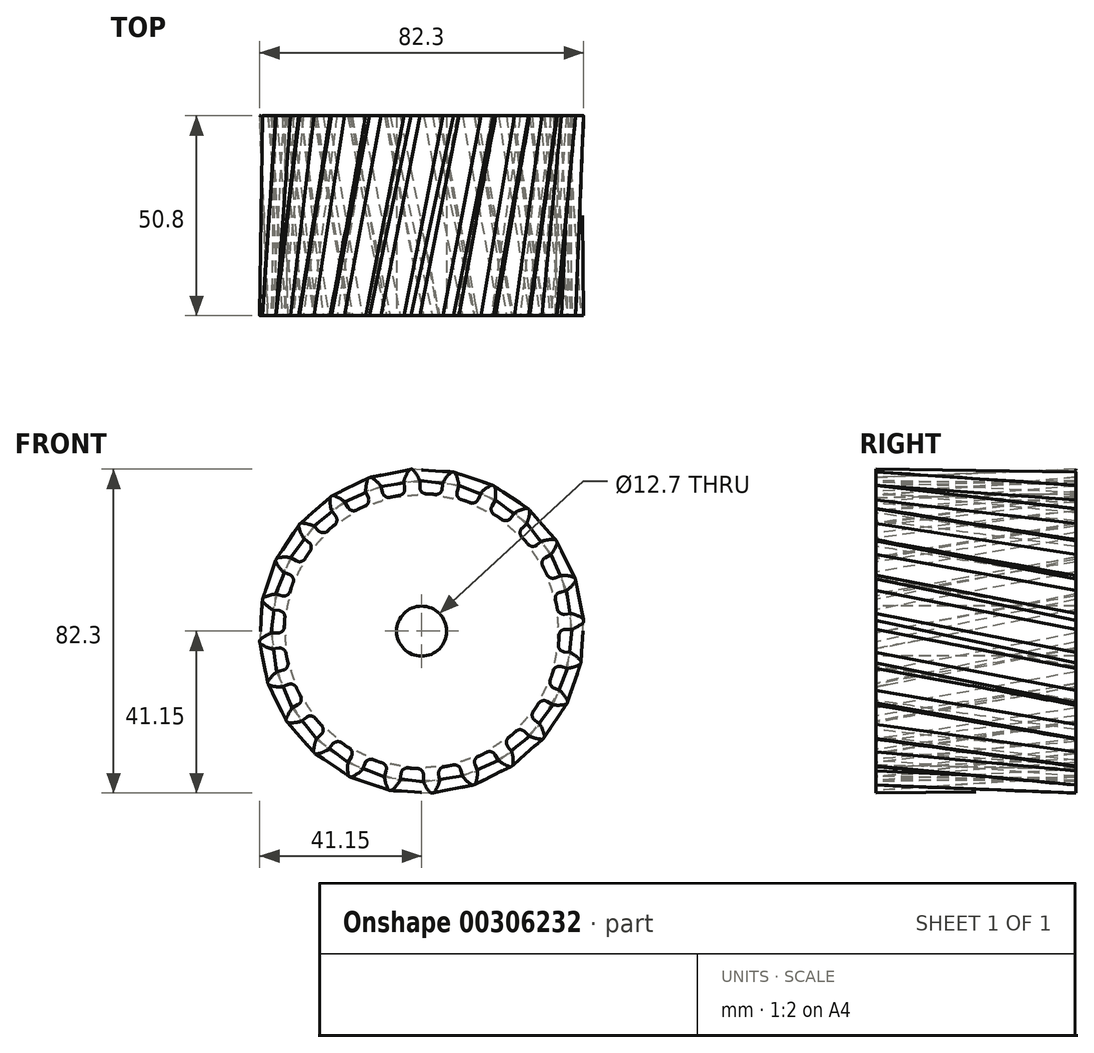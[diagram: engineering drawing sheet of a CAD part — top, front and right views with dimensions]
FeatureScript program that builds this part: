
annotation { "Feature Type Name" : "Feature", "Feature Type Description" : "" }
export const myFeature = defineFeature(function(context is Context, id is Id, definition is map)
    precondition{}
    {
        {
            var Q0;
            Q0=qCreatedBy(makeId("Front.planeOp"),FACE);
            var sketch = newSketch(context, id + "F0", { "sketchPlane" : qUnion([Q0])});
            skArc(sketch, "E0", {"start": v(-5.64, 34.47) * mm, "mid": v(-6.82, 34.25) * mm, "end": v(-7.99, 34) * mm});
            skLineSegment(sketch, "E1", {"start": v(0, 0) * mm, "end": v(-3.97, 60.48) * mm, "construction": true});
            skLineSegment(sketch, "E2", {"start": v(-2.53, 41.15) * mm, "end": v(-2.7, 41.15) * mm});
            skLineSegment(sketch, "E3", {"start": v(-0.47, 38.24) * mm, "end": v(-0.47, 36.5) * mm});
            skArc(sketch, "E4.trimOffspring", {"start": v(-0.47, 38.24) * mm, "mid": v(-1.2, 39.68) * mm, "end": v(-2.15, 40.98) * mm});
            skLineSegment(sketch, "E5.MirrorCS", {"start": v(-2.88, 41.13) * mm, "end": v(-2.7, 41.15) * mm});
            skArc(sketch, "E6.MirrorCS", {"start": v(-4.53, 37.97) * mm, "mid": v(-4, 39.5) * mm, "end": v(-3.23, 40.9) * mm});
            skLineSegment(sketch, "E7.MirrorCS", {"start": v(-4.53, 37.97) * mm, "end": v(-4.31, 36.25) * mm});
            skPoint(sketch, "E8.orphan", {"position": v(-3.52, 30.07) * mm});
            skPoint(sketch, "E9.orphan", {"position": v(-0.44, 30.27) * mm});
            skPoint(sketch, "E10.visualSharp", {"position": v(-3.1, 41.1) * mm});
            skArc(sketch, "E10.filletArc", {"start": v(-2.88, 41.13) * mm, "mid": v(-3.08, 41.06) * mm, "end": v(-3.23, 40.9) * mm});
            skPoint(sketch, "E11.visualSharp", {"position": v(-2.3, 41.15) * mm});
            skArc(sketch, "E11.filletArc", {"start": v(-2.15, 40.98) * mm, "mid": v(-2.32, 41.1) * mm, "end": v(-2.53, 41.15) * mm});
            skPoint(sketch, "E12.visualSharp", {"position": v(-4.11, 34.68) * mm});
            skArc(sketch, "E12.filletArc", {"start": v(-5.64, 34.47) * mm, "mid": v(-4.62, 35.09) * mm, "end": v(-4.31, 36.25) * mm});
            skPoint(sketch, "E13.visualSharp", {"position": v(-0.46, 34.92) * mm});
            skArc(sketch, "E13.filletArc", {"start": v(-0.47, 36.5) * mm, "mid": v(-0.01, 35.4) * mm, "end": v(1.08, 34.9) * mm});
            skLineSegment(sketch, "E14.1.0", {"start": v(-14.2, 35.5) * mm, "end": v(-13.55, 33.9) * mm});
            skArc(sketch, "E14.1.1", {"start": v(-14.37, 31.83) * mm, "mid": v(-13.54, 32.7) * mm, "end": v(-13.55, 33.9) * mm});
            skArc(sketch, "E14.1.2", {"start": v(-14.2, 35.5) * mm, "mid": v(-14.1, 37.11) * mm, "end": v(-13.7, 38.68) * mm});
            skArc(sketch, "E14.1.3", {"start": v(-13.42, 38.98) * mm, "mid": v(-13.6, 38.86) * mm, "end": v(-13.7, 38.68) * mm});
            skLineSegment(sketch, "E14.1.4", {"start": v(-13.42, 38.98) * mm, "end": v(-13.26, 39.05) * mm});
            skLineSegment(sketch, "E14.1.5", {"start": v(-13.1, 39.1) * mm, "end": v(-13.26, 39.05) * mm});
            skArc(sketch, "E14.1.6", {"start": v(-12.68, 39.03) * mm, "mid": v(-12.88, 39.1) * mm, "end": v(-13.1, 39.1) * mm});
            skArc(sketch, "E14.1.7", {"start": v(-10.35, 36.81) * mm, "mid": v(-11.42, 38.02) * mm, "end": v(-12.68, 39.03) * mm});
            skLineSegment(sketch, "E14.1.8", {"start": v(-10.35, 36.81) * mm, "end": v(-9.9, 35.14) * mm});
            skArc(sketch, "E14.1.9", {"start": v(-9.9, 35.14) * mm, "mid": v(-9.17, 34.18) * mm, "end": v(-7.99, 34) * mm});
            skLineSegment(sketch, "E14.2.0", {"start": v(-22.91, 30.62) * mm, "end": v(-21.86, 29.24) * mm});
            skArc(sketch, "E14.2.1", {"start": v(-22.12, 27.03) * mm, "mid": v(-21.54, 28.08) * mm, "end": v(-21.86, 29.24) * mm});
            skArc(sketch, "E14.2.2", {"start": v(-22.91, 30.62) * mm, "mid": v(-23.22, 32.2) * mm, "end": v(-23.25, 33.81) * mm});
            skArc(sketch, "E14.2.3", {"start": v(-23.05, 34.18) * mm, "mid": v(-23.2, 34.02) * mm, "end": v(-23.25, 33.81) * mm});
            skLineSegment(sketch, "E14.2.4", {"start": v(-23.05, 34.18) * mm, "end": v(-22.92, 34.29) * mm});
            skLineSegment(sketch, "E14.2.5", {"start": v(-22.77, 34.37) * mm, "end": v(-22.92, 34.29) * mm});
            skArc(sketch, "E14.2.6", {"start": v(-22.35, 34.42) * mm, "mid": v(-22.56, 34.44) * mm, "end": v(-22.77, 34.37) * mm});
            skArc(sketch, "E14.2.7", {"start": v(-19.53, 32.88) * mm, "mid": v(-20.87, 33.77) * mm, "end": v(-22.35, 34.42) * mm});
            skLineSegment(sketch, "E14.2.8", {"start": v(-19.53, 32.88) * mm, "end": v(-18.65, 31.38) * mm});
            skArc(sketch, "E14.2.9", {"start": v(-18.65, 31.38) * mm, "mid": v(-17.7, 30.64) * mm, "end": v(-16.51, 30.77) * mm});
            skLineSegment(sketch, "E14.3.0", {"start": v(-30.06, 23.65) * mm, "end": v(-28.68, 22.58) * mm});
            skArc(sketch, "E14.3.1", {"start": v(-28.36, 20.38) * mm, "mid": v(-28.08, 21.55) * mm, "end": v(-28.68, 22.58) * mm});
            skArc(sketch, "E14.3.2", {"start": v(-30.06, 23.65) * mm, "mid": v(-30.76, 25.1) * mm, "end": v(-31.21, 26.64) * mm});
            skArc(sketch, "E14.3.3", {"start": v(-31.12, 27.05) * mm, "mid": v(-31.2, 26.86) * mm, "end": v(-31.21, 26.64) * mm});
            skLineSegment(sketch, "E14.3.4", {"start": v(-31.12, 27.05) * mm, "end": v(-31.01, 27.19) * mm});
            skLineSegment(sketch, "E14.3.5", {"start": v(-30.89, 27.31) * mm, "end": v(-31.01, 27.19) * mm});
            skArc(sketch, "E14.3.6", {"start": v(-30.5, 27.46) * mm, "mid": v(-30.7, 27.43) * mm, "end": v(-30.89, 27.31) * mm});
            skArc(sketch, "E14.3.7", {"start": v(-27.37, 26.7) * mm, "mid": v(-28.9, 27.22) * mm, "end": v(-30.5, 27.46) * mm});
            skLineSegment(sketch, "E14.3.8", {"start": v(-27.37, 26.7) * mm, "end": v(-26.14, 25.48) * mm});
            skArc(sketch, "E14.3.9", {"start": v(-26.14, 25.48) * mm, "mid": v(-25.03, 25.02) * mm, "end": v(-23.92, 25.45) * mm});
            skLineSegment(sketch, "E14.4.0", {"start": v(-35.15, 15.06) * mm, "end": v(-33.55, 14.39) * mm});
            skArc(sketch, "E14.4.1", {"start": v(-32.67, 12.35) * mm, "mid": v(-32.7, 13.55) * mm, "end": v(-33.55, 14.39) * mm});
            skArc(sketch, "E14.4.2", {"start": v(-35.15, 15.06) * mm, "mid": v(-36.2, 16.28) * mm, "end": v(-37.04, 17.66) * mm});
            skArc(sketch, "E14.4.3", {"start": v(-37.06, 18.07) * mm, "mid": v(-37.1, 17.86) * mm, "end": v(-37.04, 17.66) * mm});
            skLineSegment(sketch, "E14.4.4", {"start": v(-37.06, 18.07) * mm, "end": v(-37, 18.24) * mm});
            skLineSegment(sketch, "E14.4.5", {"start": v(-36.9, 18.39) * mm, "end": v(-37, 18.24) * mm});
            skArc(sketch, "E14.4.6", {"start": v(-36.56, 18.63) * mm, "mid": v(-36.76, 18.54) * mm, "end": v(-36.9, 18.39) * mm});
            skArc(sketch, "E14.4.7", {"start": v(-33.35, 18.7) * mm, "mid": v(-34.96, 18.8) * mm, "end": v(-36.56, 18.63) * mm});
            skLineSegment(sketch, "E14.4.8", {"start": v(-33.35, 18.7) * mm, "end": v(-31.84, 17.85) * mm});
            skArc(sketch, "E14.4.9", {"start": v(-31.84, 17.85) * mm, "mid": v(-30.66, 17.69) * mm, "end": v(-29.69, 18.4) * mm});
            skLineSegment(sketch, "E14.5.0", {"start": v(-37.85, 5.45) * mm, "end": v(-36.13, 5.22) * mm});
            skArc(sketch, "E14.5.1", {"start": v(-34.75, 3.47) * mm, "mid": v(-35.09, 4.62) * mm, "end": v(-36.13, 5.22) * mm});
            skArc(sketch, "E14.5.2", {"start": v(-37.85, 5.45) * mm, "mid": v(-39.19, 6.35) * mm, "end": v(-40.35, 7.47) * mm});
            skArc(sketch, "E14.5.3", {"start": v(-40.47, 7.87) * mm, "mid": v(-40.45, 7.65) * mm, "end": v(-40.35, 7.47) * mm});
            skLineSegment(sketch, "E14.5.4", {"start": v(-40.47, 7.87) * mm, "end": v(-40.45, 8.04) * mm});
            skLineSegment(sketch, "E14.5.5", {"start": v(-40.4, 8.2) * mm, "end": v(-40.45, 8.04) * mm});
            skArc(sketch, "E14.5.6", {"start": v(-40.14, 8.53) * mm, "mid": v(-40.3, 8.4) * mm, "end": v(-40.4, 8.2) * mm});
            skArc(sketch, "E14.5.7", {"start": v(-37.06, 9.44) * mm, "mid": v(-38.64, 9.12) * mm, "end": v(-40.14, 8.53) * mm});
            skLineSegment(sketch, "E14.5.8", {"start": v(-37.06, 9.44) * mm, "end": v(-35.38, 9) * mm});
            skArc(sketch, "E14.5.9", {"start": v(-35.38, 9) * mm, "mid": v(-34.19, 9.15) * mm, "end": v(-33.44, 10.08) * mm});
            skLineSegment(sketch, "E14.6.0", {"start": v(-37.97, -4.53) * mm, "end": v(-36.25, -4.31) * mm});
            skArc(sketch, "E14.6.1", {"start": v(-34.47, -5.64) * mm, "mid": v(-35.09, -4.62) * mm, "end": v(-36.25, -4.31) * mm});
            skArc(sketch, "E14.6.2", {"start": v(-37.97, -4.53) * mm, "mid": v(-39.5, -4) * mm, "end": v(-40.9, -3.23) * mm});
            skArc(sketch, "E14.6.3", {"start": v(-41.13, -2.88) * mm, "mid": v(-41.06, -3.08) * mm, "end": v(-40.9, -3.23) * mm});
            skLineSegment(sketch, "E14.6.4", {"start": v(-41.13, -2.88) * mm, "end": v(-41.15, -2.7) * mm});
            skLineSegment(sketch, "E14.6.5", {"start": v(-41.15, -2.53) * mm, "end": v(-41.15, -2.7) * mm});
            skArc(sketch, "E14.6.6", {"start": v(-40.98, -2.15) * mm, "mid": v(-41.1, -2.32) * mm, "end": v(-41.15, -2.53) * mm});
            skArc(sketch, "E14.6.7", {"start": v(-38.24, -0.47) * mm, "mid": v(-39.68, -1.2) * mm, "end": v(-40.98, -2.15) * mm});
            skLineSegment(sketch, "E14.6.8", {"start": v(-38.24, -0.47) * mm, "end": v(-36.5, -0.47) * mm});
            skArc(sketch, "E14.6.9", {"start": v(-36.5, -0.47) * mm, "mid": v(-35.4, -0.01) * mm, "end": v(-34.9, 1.08) * mm});
            skLineSegment(sketch, "E14.7.0", {"start": v(-35.5, -14.2) * mm, "end": v(-33.9, -13.55) * mm});
            skArc(sketch, "E14.7.1", {"start": v(-31.83, -14.37) * mm, "mid": v(-32.7, -13.54) * mm, "end": v(-33.9, -13.55) * mm});
            skArc(sketch, "E14.7.2", {"start": v(-35.5, -14.2) * mm, "mid": v(-37.11, -14.1) * mm, "end": v(-38.68, -13.7) * mm});
            skArc(sketch, "E14.7.3", {"start": v(-38.98, -13.42) * mm, "mid": v(-38.86, -13.6) * mm, "end": v(-38.68, -13.7) * mm});
            skLineSegment(sketch, "E14.7.4", {"start": v(-38.98, -13.42) * mm, "end": v(-39.05, -13.26) * mm});
            skLineSegment(sketch, "E14.7.5", {"start": v(-39.1, -13.1) * mm, "end": v(-39.05, -13.26) * mm});
            skArc(sketch, "E14.7.6", {"start": v(-39.03, -12.68) * mm, "mid": v(-39.1, -12.88) * mm, "end": v(-39.1, -13.1) * mm});
            skArc(sketch, "E14.7.7", {"start": v(-36.81, -10.35) * mm, "mid": v(-38.02, -11.42) * mm, "end": v(-39.03, -12.68) * mm});
            skLineSegment(sketch, "E14.7.8", {"start": v(-36.81, -10.35) * mm, "end": v(-35.14, -9.9) * mm});
            skArc(sketch, "E14.7.9", {"start": v(-35.14, -9.9) * mm, "mid": v(-34.18, -9.17) * mm, "end": v(-34, -7.99) * mm});
            skLineSegment(sketch, "E14.8.0", {"start": v(-30.62, -22.91) * mm, "end": v(-29.24, -21.86) * mm});
            skArc(sketch, "E14.8.1", {"start": v(-27.03, -22.12) * mm, "mid": v(-28.08, -21.54) * mm, "end": v(-29.24, -21.86) * mm});
            skArc(sketch, "E14.8.2", {"start": v(-30.62, -22.91) * mm, "mid": v(-32.2, -23.22) * mm, "end": v(-33.81, -23.25) * mm});
            skArc(sketch, "E14.8.3", {"start": v(-34.18, -23.05) * mm, "mid": v(-34.02, -23.2) * mm, "end": v(-33.81, -23.25) * mm});
            skLineSegment(sketch, "E14.8.4", {"start": v(-34.18, -23.05) * mm, "end": v(-34.29, -22.92) * mm});
            skLineSegment(sketch, "E14.8.5", {"start": v(-34.37, -22.77) * mm, "end": v(-34.29, -22.92) * mm});
            skArc(sketch, "E14.8.6", {"start": v(-34.42, -22.35) * mm, "mid": v(-34.44, -22.56) * mm, "end": v(-34.37, -22.77) * mm});
            skArc(sketch, "E14.8.7", {"start": v(-32.88, -19.53) * mm, "mid": v(-33.77, -20.87) * mm, "end": v(-34.42, -22.35) * mm});
            skLineSegment(sketch, "E14.8.8", {"start": v(-32.88, -19.53) * mm, "end": v(-31.38, -18.65) * mm});
            skArc(sketch, "E14.8.9", {"start": v(-31.38, -18.65) * mm, "mid": v(-30.64, -17.7) * mm, "end": v(-30.77, -16.51) * mm});
            skLineSegment(sketch, "E14.9.0", {"start": v(-23.65, -30.06) * mm, "end": v(-22.58, -28.68) * mm});
            skArc(sketch, "E14.9.1", {"start": v(-20.38, -28.36) * mm, "mid": v(-21.55, -28.08) * mm, "end": v(-22.58, -28.68) * mm});
            skArc(sketch, "E14.9.2", {"start": v(-23.65, -30.06) * mm, "mid": v(-25.1, -30.76) * mm, "end": v(-26.64, -31.21) * mm});
            skArc(sketch, "E14.9.3", {"start": v(-27.05, -31.12) * mm, "mid": v(-26.86, -31.2) * mm, "end": v(-26.64, -31.21) * mm});
            skLineSegment(sketch, "E14.9.4", {"start": v(-27.05, -31.12) * mm, "end": v(-27.19, -31.01) * mm});
            skLineSegment(sketch, "E14.9.5", {"start": v(-27.31, -30.89) * mm, "end": v(-27.19, -31.01) * mm});
            skArc(sketch, "E14.9.6", {"start": v(-27.46, -30.5) * mm, "mid": v(-27.43, -30.7) * mm, "end": v(-27.31, -30.89) * mm});
            skArc(sketch, "E14.9.7", {"start": v(-26.7, -27.37) * mm, "mid": v(-27.22, -28.9) * mm, "end": v(-27.46, -30.5) * mm});
            skLineSegment(sketch, "E14.9.8", {"start": v(-26.7, -27.37) * mm, "end": v(-25.48, -26.14) * mm});
            skArc(sketch, "E14.9.9", {"start": v(-25.48, -26.14) * mm, "mid": v(-25.02, -25.03) * mm, "end": v(-25.45, -23.92) * mm});
            skLineSegment(sketch, "E14.10.0", {"start": v(-15.06, -35.15) * mm, "end": v(-14.39, -33.55) * mm});
            skArc(sketch, "E14.10.1", {"start": v(-12.35, -32.67) * mm, "mid": v(-13.55, -32.7) * mm, "end": v(-14.39, -33.55) * mm});
            skArc(sketch, "E14.10.2", {"start": v(-15.06, -35.15) * mm, "mid": v(-16.28, -36.2) * mm, "end": v(-17.66, -37.04) * mm});
            skArc(sketch, "E14.10.3", {"start": v(-18.07, -37.06) * mm, "mid": v(-17.86, -37.1) * mm, "end": v(-17.66, -37.04) * mm});
            skLineSegment(sketch, "E14.10.4", {"start": v(-18.07, -37.06) * mm, "end": v(-18.24, -37) * mm});
            skLineSegment(sketch, "E14.10.5", {"start": v(-18.39, -36.9) * mm, "end": v(-18.24, -37) * mm});
            skArc(sketch, "E14.10.6", {"start": v(-18.63, -36.56) * mm, "mid": v(-18.54, -36.76) * mm, "end": v(-18.39, -36.9) * mm});
            skArc(sketch, "E14.10.7", {"start": v(-18.7, -33.35) * mm, "mid": v(-18.8, -34.96) * mm, "end": v(-18.63, -36.56) * mm});
            skLineSegment(sketch, "E14.10.8", {"start": v(-18.7, -33.35) * mm, "end": v(-17.85, -31.84) * mm});
            skArc(sketch, "E14.10.9", {"start": v(-17.85, -31.84) * mm, "mid": v(-17.69, -30.66) * mm, "end": v(-18.4, -29.69) * mm});
            skLineSegment(sketch, "E14.11.0", {"start": v(-5.45, -37.85) * mm, "end": v(-5.22, -36.13) * mm});
            skArc(sketch, "E14.11.1", {"start": v(-3.47, -34.75) * mm, "mid": v(-4.62, -35.09) * mm, "end": v(-5.22, -36.13) * mm});
            skArc(sketch, "E14.11.2", {"start": v(-5.45, -37.85) * mm, "mid": v(-6.35, -39.19) * mm, "end": v(-7.47, -40.35) * mm});
            skArc(sketch, "E14.11.3", {"start": v(-7.87, -40.47) * mm, "mid": v(-7.65, -40.45) * mm, "end": v(-7.47, -40.35) * mm});
            skLineSegment(sketch, "E14.11.4", {"start": v(-7.87, -40.47) * mm, "end": v(-8.04, -40.45) * mm});
            skLineSegment(sketch, "E14.11.5", {"start": v(-8.2, -40.4) * mm, "end": v(-8.04, -40.45) * mm});
            skArc(sketch, "E14.11.6", {"start": v(-8.53, -40.14) * mm, "mid": v(-8.4, -40.3) * mm, "end": v(-8.2, -40.4) * mm});
            skArc(sketch, "E14.11.7", {"start": v(-9.44, -37.06) * mm, "mid": v(-9.12, -38.64) * mm, "end": v(-8.53, -40.14) * mm});
            skLineSegment(sketch, "E14.11.8", {"start": v(-9.44, -37.06) * mm, "end": v(-9, -35.38) * mm});
            skArc(sketch, "E14.11.9", {"start": v(-9, -35.38) * mm, "mid": v(-9.15, -34.19) * mm, "end": v(-10.08, -33.44) * mm});
            skLineSegment(sketch, "E14.12.0", {"start": v(4.53, -37.97) * mm, "end": v(4.31, -36.25) * mm});
            skArc(sketch, "E14.12.1", {"start": v(5.64, -34.47) * mm, "mid": v(4.62, -35.09) * mm, "end": v(4.31, -36.25) * mm});
            skArc(sketch, "E14.12.2", {"start": v(4.53, -37.97) * mm, "mid": v(4, -39.5) * mm, "end": v(3.23, -40.9) * mm});
            skArc(sketch, "E14.12.3", {"start": v(2.88, -41.13) * mm, "mid": v(3.08, -41.06) * mm, "end": v(3.23, -40.9) * mm});
            skLineSegment(sketch, "E14.12.4", {"start": v(2.88, -41.13) * mm, "end": v(2.7, -41.15) * mm});
            skLineSegment(sketch, "E14.12.5", {"start": v(2.53, -41.15) * mm, "end": v(2.7, -41.15) * mm});
            skArc(sketch, "E14.12.6", {"start": v(2.15, -40.98) * mm, "mid": v(2.32, -41.1) * mm, "end": v(2.53, -41.15) * mm});
            skArc(sketch, "E14.12.7", {"start": v(0.47, -38.24) * mm, "mid": v(1.2, -39.68) * mm, "end": v(2.15, -40.98) * mm});
            skLineSegment(sketch, "E14.12.8", {"start": v(0.47, -38.24) * mm, "end": v(0.47, -36.5) * mm});
            skArc(sketch, "E14.12.9", {"start": v(0.47, -36.5) * mm, "mid": v(0.01, -35.4) * mm, "end": v(-1.08, -34.9) * mm});
            skLineSegment(sketch, "E14.13.0", {"start": v(14.2, -35.5) * mm, "end": v(13.55, -33.9) * mm});
            skArc(sketch, "E14.13.1", {"start": v(14.37, -31.83) * mm, "mid": v(13.54, -32.7) * mm, "end": v(13.55, -33.9) * mm});
            skArc(sketch, "E14.13.2", {"start": v(14.2, -35.5) * mm, "mid": v(14.1, -37.11) * mm, "end": v(13.7, -38.68) * mm});
            skArc(sketch, "E14.13.3", {"start": v(13.42, -38.98) * mm, "mid": v(13.6, -38.86) * mm, "end": v(13.7, -38.68) * mm});
            skLineSegment(sketch, "E14.13.4", {"start": v(13.42, -38.98) * mm, "end": v(13.26, -39.05) * mm});
            skLineSegment(sketch, "E14.13.5", {"start": v(13.1, -39.1) * mm, "end": v(13.26, -39.05) * mm});
            skArc(sketch, "E14.13.6", {"start": v(12.68, -39.03) * mm, "mid": v(12.88, -39.1) * mm, "end": v(13.1, -39.1) * mm});
            skArc(sketch, "E14.13.7", {"start": v(10.35, -36.81) * mm, "mid": v(11.42, -38.02) * mm, "end": v(12.68, -39.03) * mm});
            skLineSegment(sketch, "E14.13.8", {"start": v(10.35, -36.81) * mm, "end": v(9.9, -35.14) * mm});
            skArc(sketch, "E14.13.9", {"start": v(9.9, -35.14) * mm, "mid": v(9.17, -34.18) * mm, "end": v(7.99, -34) * mm});
            skLineSegment(sketch, "E14.14.0", {"start": v(22.91, -30.62) * mm, "end": v(21.86, -29.24) * mm});
            skArc(sketch, "E14.14.1", {"start": v(22.12, -27.03) * mm, "mid": v(21.54, -28.08) * mm, "end": v(21.86, -29.24) * mm});
            skArc(sketch, "E14.14.2", {"start": v(22.91, -30.62) * mm, "mid": v(23.22, -32.2) * mm, "end": v(23.25, -33.81) * mm});
            skArc(sketch, "E14.14.3", {"start": v(23.05, -34.18) * mm, "mid": v(23.2, -34.02) * mm, "end": v(23.25, -33.81) * mm});
            skLineSegment(sketch, "E14.14.4", {"start": v(23.05, -34.18) * mm, "end": v(22.92, -34.29) * mm});
            skLineSegment(sketch, "E14.14.5", {"start": v(22.77, -34.37) * mm, "end": v(22.92, -34.29) * mm});
            skArc(sketch, "E14.14.6", {"start": v(22.35, -34.42) * mm, "mid": v(22.56, -34.44) * mm, "end": v(22.77, -34.37) * mm});
            skArc(sketch, "E14.14.7", {"start": v(19.53, -32.88) * mm, "mid": v(20.87, -33.77) * mm, "end": v(22.35, -34.42) * mm});
            skLineSegment(sketch, "E14.14.8", {"start": v(19.53, -32.88) * mm, "end": v(18.65, -31.38) * mm});
            skArc(sketch, "E14.14.9", {"start": v(18.65, -31.38) * mm, "mid": v(17.7, -30.64) * mm, "end": v(16.51, -30.77) * mm});
            skLineSegment(sketch, "E14.15.0", {"start": v(30.06, -23.65) * mm, "end": v(28.68, -22.58) * mm});
            skArc(sketch, "E14.15.1", {"start": v(28.36, -20.38) * mm, "mid": v(28.08, -21.55) * mm, "end": v(28.68, -22.58) * mm});
            skArc(sketch, "E14.15.2", {"start": v(30.06, -23.65) * mm, "mid": v(30.76, -25.1) * mm, "end": v(31.21, -26.64) * mm});
            skArc(sketch, "E14.15.3", {"start": v(31.12, -27.05) * mm, "mid": v(31.2, -26.86) * mm, "end": v(31.21, -26.64) * mm});
            skLineSegment(sketch, "E14.15.4", {"start": v(31.12, -27.05) * mm, "end": v(31.01, -27.19) * mm});
            skLineSegment(sketch, "E14.15.5", {"start": v(30.89, -27.31) * mm, "end": v(31.01, -27.19) * mm});
            skArc(sketch, "E14.15.6", {"start": v(30.5, -27.46) * mm, "mid": v(30.7, -27.43) * mm, "end": v(30.89, -27.31) * mm});
            skArc(sketch, "E14.15.7", {"start": v(27.37, -26.7) * mm, "mid": v(28.9, -27.22) * mm, "end": v(30.5, -27.46) * mm});
            skLineSegment(sketch, "E14.15.8", {"start": v(27.37, -26.7) * mm, "end": v(26.14, -25.48) * mm});
            skArc(sketch, "E14.15.9", {"start": v(26.14, -25.48) * mm, "mid": v(25.03, -25.02) * mm, "end": v(23.92, -25.45) * mm});
            skLineSegment(sketch, "E14.16.0", {"start": v(35.15, -15.06) * mm, "end": v(33.55, -14.39) * mm});
            skArc(sketch, "E14.16.1", {"start": v(32.67, -12.35) * mm, "mid": v(32.7, -13.55) * mm, "end": v(33.55, -14.39) * mm});
            skArc(sketch, "E14.16.2", {"start": v(35.15, -15.06) * mm, "mid": v(36.2, -16.28) * mm, "end": v(37.04, -17.66) * mm});
            skArc(sketch, "E14.16.3", {"start": v(37.06, -18.07) * mm, "mid": v(37.1, -17.86) * mm, "end": v(37.04, -17.66) * mm});
            skLineSegment(sketch, "E14.16.4", {"start": v(37.06, -18.07) * mm, "end": v(37, -18.24) * mm});
            skLineSegment(sketch, "E14.16.5", {"start": v(36.9, -18.39) * mm, "end": v(37, -18.24) * mm});
            skArc(sketch, "E14.16.6", {"start": v(36.56, -18.63) * mm, "mid": v(36.76, -18.54) * mm, "end": v(36.9, -18.39) * mm});
            skArc(sketch, "E14.16.7", {"start": v(33.35, -18.7) * mm, "mid": v(34.96, -18.8) * mm, "end": v(36.56, -18.63) * mm});
            skLineSegment(sketch, "E14.16.8", {"start": v(33.35, -18.7) * mm, "end": v(31.84, -17.85) * mm});
            skArc(sketch, "E14.16.9", {"start": v(31.84, -17.85) * mm, "mid": v(30.66, -17.69) * mm, "end": v(29.69, -18.4) * mm});
            skLineSegment(sketch, "E14.17.0", {"start": v(37.85, -5.45) * mm, "end": v(36.13, -5.22) * mm});
            skArc(sketch, "E14.17.1", {"start": v(34.75, -3.47) * mm, "mid": v(35.09, -4.62) * mm, "end": v(36.13, -5.22) * mm});
            skArc(sketch, "E14.17.2", {"start": v(37.85, -5.45) * mm, "mid": v(39.19, -6.35) * mm, "end": v(40.35, -7.47) * mm});
            skArc(sketch, "E14.17.3", {"start": v(40.47, -7.87) * mm, "mid": v(40.45, -7.65) * mm, "end": v(40.35, -7.47) * mm});
            skLineSegment(sketch, "E14.17.4", {"start": v(40.47, -7.87) * mm, "end": v(40.45, -8.04) * mm});
            skLineSegment(sketch, "E14.17.5", {"start": v(40.4, -8.2) * mm, "end": v(40.45, -8.04) * mm});
            skArc(sketch, "E14.17.6", {"start": v(40.14, -8.53) * mm, "mid": v(40.3, -8.4) * mm, "end": v(40.4, -8.2) * mm});
            skArc(sketch, "E14.17.7", {"start": v(37.06, -9.44) * mm, "mid": v(38.64, -9.12) * mm, "end": v(40.14, -8.53) * mm});
            skLineSegment(sketch, "E14.17.8", {"start": v(37.06, -9.44) * mm, "end": v(35.38, -9) * mm});
            skArc(sketch, "E14.17.9", {"start": v(35.38, -9) * mm, "mid": v(34.19, -9.15) * mm, "end": v(33.44, -10.08) * mm});
            skLineSegment(sketch, "E14.18.0", {"start": v(37.97, 4.53) * mm, "end": v(36.25, 4.31) * mm});
            skArc(sketch, "E14.18.1", {"start": v(34.47, 5.64) * mm, "mid": v(35.09, 4.62) * mm, "end": v(36.25, 4.31) * mm});
            skArc(sketch, "E14.18.2", {"start": v(37.97, 4.53) * mm, "mid": v(39.5, 4) * mm, "end": v(40.9, 3.23) * mm});
            skArc(sketch, "E14.18.3", {"start": v(41.13, 2.88) * mm, "mid": v(41.06, 3.08) * mm, "end": v(40.9, 3.23) * mm});
            skLineSegment(sketch, "E14.18.4", {"start": v(41.13, 2.88) * mm, "end": v(41.15, 2.7) * mm});
            skLineSegment(sketch, "E14.18.5", {"start": v(41.15, 2.53) * mm, "end": v(41.15, 2.7) * mm});
            skArc(sketch, "E14.18.6", {"start": v(40.98, 2.15) * mm, "mid": v(41.1, 2.32) * mm, "end": v(41.15, 2.53) * mm});
            skArc(sketch, "E14.18.7", {"start": v(38.24, 0.47) * mm, "mid": v(39.68, 1.2) * mm, "end": v(40.98, 2.15) * mm});
            skLineSegment(sketch, "E14.18.8", {"start": v(38.24, 0.47) * mm, "end": v(36.5, 0.47) * mm});
            skArc(sketch, "E14.18.9", {"start": v(36.5, 0.47) * mm, "mid": v(35.4, 0.01) * mm, "end": v(34.9, -1.08) * mm});
            skLineSegment(sketch, "E14.19.0", {"start": v(35.5, 14.2) * mm, "end": v(33.9, 13.55) * mm});
            skArc(sketch, "E14.19.1", {"start": v(31.83, 14.37) * mm, "mid": v(32.7, 13.54) * mm, "end": v(33.9, 13.55) * mm});
            skArc(sketch, "E14.19.2", {"start": v(35.5, 14.2) * mm, "mid": v(37.11, 14.1) * mm, "end": v(38.68, 13.7) * mm});
            skArc(sketch, "E14.19.3", {"start": v(38.98, 13.42) * mm, "mid": v(38.86, 13.6) * mm, "end": v(38.68, 13.7) * mm});
            skLineSegment(sketch, "E14.19.4", {"start": v(38.98, 13.42) * mm, "end": v(39.05, 13.26) * mm});
            skLineSegment(sketch, "E14.19.5", {"start": v(39.1, 13.1) * mm, "end": v(39.05, 13.26) * mm});
            skArc(sketch, "E14.19.6", {"start": v(39.03, 12.68) * mm, "mid": v(39.1, 12.88) * mm, "end": v(39.1, 13.1) * mm});
            skArc(sketch, "E14.19.7", {"start": v(36.81, 10.35) * mm, "mid": v(38.02, 11.42) * mm, "end": v(39.03, 12.68) * mm});
            skLineSegment(sketch, "E14.19.8", {"start": v(36.81, 10.35) * mm, "end": v(35.14, 9.9) * mm});
            skArc(sketch, "E14.19.9", {"start": v(35.14, 9.9) * mm, "mid": v(34.18, 9.17) * mm, "end": v(34, 7.99) * mm});
            skLineSegment(sketch, "E14.20.0", {"start": v(30.62, 22.91) * mm, "end": v(29.24, 21.86) * mm});
            skArc(sketch, "E14.20.1", {"start": v(27.03, 22.12) * mm, "mid": v(28.08, 21.54) * mm, "end": v(29.24, 21.86) * mm});
            skArc(sketch, "E14.20.2", {"start": v(30.62, 22.91) * mm, "mid": v(32.2, 23.22) * mm, "end": v(33.81, 23.25) * mm});
            skArc(sketch, "E14.20.3", {"start": v(34.18, 23.05) * mm, "mid": v(34.02, 23.2) * mm, "end": v(33.81, 23.25) * mm});
            skLineSegment(sketch, "E14.20.4", {"start": v(34.18, 23.05) * mm, "end": v(34.29, 22.92) * mm});
            skLineSegment(sketch, "E14.20.5", {"start": v(34.37, 22.77) * mm, "end": v(34.29, 22.92) * mm});
            skArc(sketch, "E14.20.6", {"start": v(34.42, 22.35) * mm, "mid": v(34.44, 22.56) * mm, "end": v(34.37, 22.77) * mm});
            skArc(sketch, "E14.20.7", {"start": v(32.88, 19.53) * mm, "mid": v(33.77, 20.87) * mm, "end": v(34.42, 22.35) * mm});
            skLineSegment(sketch, "E14.20.8", {"start": v(32.88, 19.53) * mm, "end": v(31.38, 18.65) * mm});
            skArc(sketch, "E14.20.9", {"start": v(31.38, 18.65) * mm, "mid": v(30.64, 17.7) * mm, "end": v(30.77, 16.51) * mm});
            skLineSegment(sketch, "E14.21.0", {"start": v(23.65, 30.06) * mm, "end": v(22.58, 28.68) * mm});
            skArc(sketch, "E14.21.1", {"start": v(20.38, 28.36) * mm, "mid": v(21.55, 28.08) * mm, "end": v(22.58, 28.68) * mm});
            skArc(sketch, "E14.21.2", {"start": v(23.65, 30.06) * mm, "mid": v(25.1, 30.76) * mm, "end": v(26.64, 31.21) * mm});
            skArc(sketch, "E14.21.3", {"start": v(27.05, 31.12) * mm, "mid": v(26.86, 31.2) * mm, "end": v(26.64, 31.21) * mm});
            skLineSegment(sketch, "E14.21.4", {"start": v(27.05, 31.12) * mm, "end": v(27.19, 31.01) * mm});
            skLineSegment(sketch, "E14.21.5", {"start": v(27.31, 30.89) * mm, "end": v(27.19, 31.01) * mm});
            skArc(sketch, "E14.21.6", {"start": v(27.46, 30.5) * mm, "mid": v(27.43, 30.7) * mm, "end": v(27.31, 30.89) * mm});
            skArc(sketch, "E14.21.7", {"start": v(26.7, 27.37) * mm, "mid": v(27.22, 28.9) * mm, "end": v(27.46, 30.5) * mm});
            skLineSegment(sketch, "E14.21.8", {"start": v(26.7, 27.37) * mm, "end": v(25.48, 26.14) * mm});
            skArc(sketch, "E14.21.9", {"start": v(25.48, 26.14) * mm, "mid": v(25.02, 25.03) * mm, "end": v(25.45, 23.92) * mm});
            skLineSegment(sketch, "E14.22.0", {"start": v(15.06, 35.15) * mm, "end": v(14.39, 33.55) * mm});
            skArc(sketch, "E14.22.1", {"start": v(12.35, 32.67) * mm, "mid": v(13.55, 32.7) * mm, "end": v(14.39, 33.55) * mm});
            skArc(sketch, "E14.22.2", {"start": v(15.06, 35.15) * mm, "mid": v(16.28, 36.2) * mm, "end": v(17.66, 37.04) * mm});
            skArc(sketch, "E14.22.3", {"start": v(18.07, 37.06) * mm, "mid": v(17.86, 37.1) * mm, "end": v(17.66, 37.04) * mm});
            skLineSegment(sketch, "E14.22.4", {"start": v(18.07, 37.06) * mm, "end": v(18.24, 37) * mm});
            skLineSegment(sketch, "E14.22.5", {"start": v(18.39, 36.9) * mm, "end": v(18.24, 37) * mm});
            skArc(sketch, "E14.22.6", {"start": v(18.63, 36.56) * mm, "mid": v(18.54, 36.76) * mm, "end": v(18.39, 36.9) * mm});
            skArc(sketch, "E14.22.7", {"start": v(18.7, 33.35) * mm, "mid": v(18.8, 34.96) * mm, "end": v(18.63, 36.56) * mm});
            skLineSegment(sketch, "E14.22.8", {"start": v(18.7, 33.35) * mm, "end": v(17.85, 31.84) * mm});
            skArc(sketch, "E14.22.9", {"start": v(17.85, 31.84) * mm, "mid": v(17.69, 30.66) * mm, "end": v(18.4, 29.69) * mm});
            skLineSegment(sketch, "E14.23.0", {"start": v(5.45, 37.85) * mm, "end": v(5.22, 36.13) * mm});
            skArc(sketch, "E14.23.1", {"start": v(3.47, 34.75) * mm, "mid": v(4.62, 35.09) * mm, "end": v(5.22, 36.13) * mm});
            skArc(sketch, "E14.23.2", {"start": v(5.45, 37.85) * mm, "mid": v(6.35, 39.19) * mm, "end": v(7.47, 40.35) * mm});
            skArc(sketch, "E14.23.3", {"start": v(7.87, 40.47) * mm, "mid": v(7.65, 40.45) * mm, "end": v(7.47, 40.35) * mm});
            skLineSegment(sketch, "E14.23.4", {"start": v(7.87, 40.47) * mm, "end": v(8.04, 40.45) * mm});
            skLineSegment(sketch, "E14.23.5", {"start": v(8.2, 40.4) * mm, "end": v(8.04, 40.45) * mm});
            skArc(sketch, "E14.23.6", {"start": v(8.53, 40.14) * mm, "mid": v(8.4, 40.3) * mm, "end": v(8.2, 40.4) * mm});
            skArc(sketch, "E14.23.7", {"start": v(9.44, 37.06) * mm, "mid": v(9.12, 38.64) * mm, "end": v(8.53, 40.14) * mm});
            skLineSegment(sketch, "E14.23.8", {"start": v(9.44, 37.06) * mm, "end": v(9, 35.38) * mm});
            skArc(sketch, "E14.23.9", {"start": v(9, 35.38) * mm, "mid": v(9.15, 34.19) * mm, "end": v(10.08, 33.44) * mm});
            skArc(sketch, "E15.trimOffspring", {"start": v(-14.37, 31.83) * mm, "mid": v(-15.45, 31.32) * mm, "end": v(-16.51, 30.77) * mm});
            skArc(sketch, "E16.trimOffspring", {"start": v(-22.12, 27.03) * mm, "mid": v(-23.03, 26.25) * mm, "end": v(-23.92, 25.45) * mm});
            skArc(sketch, "E17.trimOffspring", {"start": v(-28.36, 20.38) * mm, "mid": v(-29.04, 19.4) * mm, "end": v(-29.69, 18.4) * mm});
            skArc(sketch, "E18.trimOffspring", {"start": v(-32.67, 12.35) * mm, "mid": v(-33.07, 11.22) * mm, "end": v(-33.44, 10.08) * mm});
            skArc(sketch, "E19.trimOffspring", {"start": v(-34.75, 3.47) * mm, "mid": v(-34.85, 2.28) * mm, "end": v(-34.9, 1.08) * mm});
            skArc(sketch, "E20.trimOffspring", {"start": v(-34.47, -5.64) * mm, "mid": v(-34.25, -6.82) * mm, "end": v(-34, -7.99) * mm});
            skArc(sketch, "E21.trimOffspring", {"start": v(-31.83, -14.37) * mm, "mid": v(-31.32, -15.45) * mm, "end": v(-30.77, -16.51) * mm});
            skArc(sketch, "E22.trimOffspring", {"start": v(-27.03, -22.12) * mm, "mid": v(-26.25, -23.03) * mm, "end": v(-25.45, -23.92) * mm});
            skArc(sketch, "E23.trimOffspring", {"start": v(-20.38, -28.36) * mm, "mid": v(-19.4, -29.04) * mm, "end": v(-18.4, -29.69) * mm});
            skArc(sketch, "E24.trimOffspring", {"start": v(-12.35, -32.67) * mm, "mid": v(-11.22, -33.07) * mm, "end": v(-10.08, -33.44) * mm});
            skArc(sketch, "E25.trimOffspring", {"start": v(-3.47, -34.75) * mm, "mid": v(-2.28, -34.85) * mm, "end": v(-1.08, -34.9) * mm});
            skArc(sketch, "E26.trimOffspring", {"start": v(5.64, -34.47) * mm, "mid": v(6.82, -34.25) * mm, "end": v(7.99, -34) * mm});
            skArc(sketch, "E27.trimOffspring", {"start": v(14.37, -31.83) * mm, "mid": v(15.45, -31.32) * mm, "end": v(16.51, -30.77) * mm});
            skArc(sketch, "E28.trimOffspring", {"start": v(22.12, -27.03) * mm, "mid": v(23.03, -26.25) * mm, "end": v(23.92, -25.45) * mm});
            skArc(sketch, "E29.trimOffspring", {"start": v(28.36, -20.38) * mm, "mid": v(29.04, -19.4) * mm, "end": v(29.69, -18.4) * mm});
            skArc(sketch, "E30.trimOffspring", {"start": v(32.67, -12.35) * mm, "mid": v(33.07, -11.22) * mm, "end": v(33.44, -10.08) * mm});
            skArc(sketch, "E31.trimOffspring", {"start": v(34.75, -3.47) * mm, "mid": v(34.85, -2.28) * mm, "end": v(34.9, -1.08) * mm});
            skArc(sketch, "E32.trimOffspring", {"start": v(34.47, 5.64) * mm, "mid": v(34.25, 6.82) * mm, "end": v(34, 7.99) * mm});
            skArc(sketch, "E33.trimOffspring", {"start": v(31.83, 14.37) * mm, "mid": v(31.32, 15.45) * mm, "end": v(30.77, 16.51) * mm});
            skArc(sketch, "E34.trimOffspring", {"start": v(27.03, 22.12) * mm, "mid": v(26.25, 23.03) * mm, "end": v(25.45, 23.92) * mm});
            skArc(sketch, "E35.trimOffspring", {"start": v(20.38, 28.36) * mm, "mid": v(19.4, 29.04) * mm, "end": v(18.4, 29.69) * mm});
            skArc(sketch, "E36.trimOffspring", {"start": v(12.35, 32.67) * mm, "mid": v(11.22, 33.07) * mm, "end": v(10.08, 33.44) * mm});
            skArc(sketch, "E37.trimOffspring", {"start": v(3.47, 34.75) * mm, "mid": v(2.28, 34.85) * mm, "end": v(1.08, 34.9) * mm});
            skSolve(sketch);
        }
        {
            var Q0;
            Q0=makeQuery(id+"F0.imprint","IMPRINT",FACE,{"disambiguationData":[TD([[makeQuery(id+"F0.imprint","IMPRINT",EDGE,{"derivedFrom":sQuery(id+"F0.wireOp",EDGE,"E2")}),1.0]])]});
            cPlane(context, id + "F1", {"entities" : qUnion([Q0]), "cplaneType" : CPlaneType.OFFSET, "offset" : 50.8 * mm, "width" : 152.4 * mm, "height" : 152.4 * mm});
        }
        {
            var Q0;
            Q0=qCreatedBy(id+"F1.planeOp",FACE);
            var sketch = newSketch(context, id + "F2", { "sketchPlane" : qUnion([Q0])});
            skArc(sketch, "E38", {"start": v(-5.64, 34.47) * mm, "mid": v(-6.82, 34.25) * mm, "end": v(-7.99, 34) * mm});
            skLineSegment(sketch, "E39", {"start": v(0, 0) * mm, "end": v(-3.74, 57) * mm, "construction": true});
            skLineSegment(sketch, "E40", {"start": v(-2.53, 41.15) * mm, "end": v(-2.7, 41.15) * mm});
            skLineSegment(sketch, "E41", {"start": v(-0.47, 38.24) * mm, "end": v(-0.47, 36.5) * mm});
            skArc(sketch, "E42.trimOffspring", {"start": v(-0.47, 38.24) * mm, "mid": v(-1.2, 39.68) * mm, "end": v(-2.15, 40.98) * mm});
            skLineSegment(sketch, "E43.MirrorCS", {"start": v(-2.88, 41.13) * mm, "end": v(-2.7, 41.15) * mm});
            skArc(sketch, "E44.MirrorCS", {"start": v(-4.53, 37.97) * mm, "mid": v(-4, 39.5) * mm, "end": v(-3.23, 40.9) * mm});
            skLineSegment(sketch, "E45.MirrorCS", {"start": v(-4.53, 37.97) * mm, "end": v(-4.31, 36.25) * mm});
            skPoint(sketch, "E46.orphan", {"position": v(-3.9, 33.09) * mm});
            skPoint(sketch, "E47.orphan", {"position": v(-0.45, 33.31) * mm});
            skPoint(sketch, "E48.visualSharp", {"position": v(-3.1, 41.1) * mm});
            skArc(sketch, "E48.filletArc", {"start": v(-2.88, 41.13) * mm, "mid": v(-3.08, 41.06) * mm, "end": v(-3.23, 40.9) * mm});
            skPoint(sketch, "E49.visualSharp", {"position": v(-4.11, 34.68) * mm});
            skArc(sketch, "E49.filletArc", {"start": v(-5.64, 34.47) * mm, "mid": v(-4.62, 35.09) * mm, "end": v(-4.31, 36.25) * mm});
            skPoint(sketch, "E50.visualSharp", {"position": v(-0.46, 34.92) * mm});
            skArc(sketch, "E50.filletArc", {"start": v(-0.47, 36.5) * mm, "mid": v(-0.01, 35.4) * mm, "end": v(1.08, 34.9) * mm});
            skPoint(sketch, "E51.visualSharp", {"position": v(-2.3, 41.15) * mm});
            skArc(sketch, "E51.filletArc", {"start": v(-2.15, 40.98) * mm, "mid": v(-2.32, 41.1) * mm, "end": v(-2.53, 41.15) * mm});
            skArc(sketch, "E52.1.0", {"start": v(-14.37, 31.83) * mm, "mid": v(-13.54, 32.7) * mm, "end": v(-13.55, 33.9) * mm});
            skLineSegment(sketch, "E52.1.1", {"start": v(-14.2, 35.5) * mm, "end": v(-13.55, 33.9) * mm});
            skArc(sketch, "E52.1.2", {"start": v(-14.2, 35.5) * mm, "mid": v(-14.1, 37.11) * mm, "end": v(-13.7, 38.68) * mm});
            skArc(sketch, "E52.1.3", {"start": v(-13.42, 38.98) * mm, "mid": v(-13.6, 38.86) * mm, "end": v(-13.7, 38.68) * mm});
            skLineSegment(sketch, "E52.1.4", {"start": v(-13.42, 38.98) * mm, "end": v(-13.26, 39.05) * mm});
            skLineSegment(sketch, "E52.1.5", {"start": v(-13.1, 39.1) * mm, "end": v(-13.26, 39.05) * mm});
            skArc(sketch, "E52.1.6", {"start": v(-12.68, 39.03) * mm, "mid": v(-12.88, 39.1) * mm, "end": v(-13.1, 39.1) * mm});
            skArc(sketch, "E52.1.7", {"start": v(-10.35, 36.81) * mm, "mid": v(-11.42, 38.02) * mm, "end": v(-12.68, 39.03) * mm});
            skLineSegment(sketch, "E52.1.8", {"start": v(-10.35, 36.81) * mm, "end": v(-9.9, 35.14) * mm});
            skArc(sketch, "E52.1.9", {"start": v(-9.9, 35.14) * mm, "mid": v(-9.17, 34.18) * mm, "end": v(-7.99, 34) * mm});
            skArc(sketch, "E52.2.0", {"start": v(-22.12, 27.03) * mm, "mid": v(-21.54, 28.08) * mm, "end": v(-21.86, 29.24) * mm});
            skLineSegment(sketch, "E52.2.1", {"start": v(-22.91, 30.62) * mm, "end": v(-21.86, 29.24) * mm});
            skArc(sketch, "E52.2.2", {"start": v(-22.91, 30.62) * mm, "mid": v(-23.22, 32.2) * mm, "end": v(-23.25, 33.81) * mm});
            skArc(sketch, "E52.2.3", {"start": v(-23.05, 34.18) * mm, "mid": v(-23.2, 34.02) * mm, "end": v(-23.25, 33.81) * mm});
            skLineSegment(sketch, "E52.2.4", {"start": v(-23.05, 34.18) * mm, "end": v(-22.92, 34.29) * mm});
            skLineSegment(sketch, "E52.2.5", {"start": v(-22.77, 34.37) * mm, "end": v(-22.92, 34.29) * mm});
            skArc(sketch, "E52.2.6", {"start": v(-22.35, 34.42) * mm, "mid": v(-22.56, 34.44) * mm, "end": v(-22.77, 34.37) * mm});
            skArc(sketch, "E52.2.7", {"start": v(-19.53, 32.88) * mm, "mid": v(-20.87, 33.77) * mm, "end": v(-22.35, 34.42) * mm});
            skLineSegment(sketch, "E52.2.8", {"start": v(-19.53, 32.88) * mm, "end": v(-18.65, 31.38) * mm});
            skArc(sketch, "E52.2.9", {"start": v(-18.65, 31.38) * mm, "mid": v(-17.7, 30.64) * mm, "end": v(-16.51, 30.77) * mm});
            skArc(sketch, "E52.3.0", {"start": v(-28.36, 20.38) * mm, "mid": v(-28.08, 21.55) * mm, "end": v(-28.68, 22.58) * mm});
            skLineSegment(sketch, "E52.3.1", {"start": v(-30.06, 23.65) * mm, "end": v(-28.68, 22.58) * mm});
            skArc(sketch, "E52.3.2", {"start": v(-30.06, 23.65) * mm, "mid": v(-30.76, 25.1) * mm, "end": v(-31.21, 26.64) * mm});
            skArc(sketch, "E52.3.3", {"start": v(-31.12, 27.05) * mm, "mid": v(-31.2, 26.86) * mm, "end": v(-31.21, 26.64) * mm});
            skLineSegment(sketch, "E52.3.4", {"start": v(-31.12, 27.05) * mm, "end": v(-31.01, 27.19) * mm});
            skLineSegment(sketch, "E52.3.5", {"start": v(-30.89, 27.31) * mm, "end": v(-31.01, 27.19) * mm});
            skArc(sketch, "E52.3.6", {"start": v(-30.5, 27.46) * mm, "mid": v(-30.7, 27.43) * mm, "end": v(-30.89, 27.31) * mm});
            skArc(sketch, "E52.3.7", {"start": v(-27.37, 26.7) * mm, "mid": v(-28.9, 27.22) * mm, "end": v(-30.5, 27.46) * mm});
            skLineSegment(sketch, "E52.3.8", {"start": v(-27.37, 26.7) * mm, "end": v(-26.14, 25.48) * mm});
            skArc(sketch, "E52.3.9", {"start": v(-26.14, 25.48) * mm, "mid": v(-25.03, 25.02) * mm, "end": v(-23.92, 25.45) * mm});
            skArc(sketch, "E52.4.0", {"start": v(-32.67, 12.35) * mm, "mid": v(-32.7, 13.55) * mm, "end": v(-33.55, 14.39) * mm});
            skLineSegment(sketch, "E52.4.1", {"start": v(-35.15, 15.06) * mm, "end": v(-33.55, 14.39) * mm});
            skArc(sketch, "E52.4.2", {"start": v(-35.15, 15.06) * mm, "mid": v(-36.2, 16.28) * mm, "end": v(-37.04, 17.66) * mm});
            skArc(sketch, "E52.4.3", {"start": v(-37.06, 18.07) * mm, "mid": v(-37.1, 17.86) * mm, "end": v(-37.04, 17.66) * mm});
            skLineSegment(sketch, "E52.4.4", {"start": v(-37.06, 18.07) * mm, "end": v(-37, 18.24) * mm});
            skLineSegment(sketch, "E52.4.5", {"start": v(-36.9, 18.39) * mm, "end": v(-37, 18.24) * mm});
            skArc(sketch, "E52.4.6", {"start": v(-36.56, 18.63) * mm, "mid": v(-36.76, 18.54) * mm, "end": v(-36.9, 18.39) * mm});
            skArc(sketch, "E52.4.7", {"start": v(-33.35, 18.7) * mm, "mid": v(-34.96, 18.8) * mm, "end": v(-36.56, 18.63) * mm});
            skLineSegment(sketch, "E52.4.8", {"start": v(-33.35, 18.7) * mm, "end": v(-31.84, 17.85) * mm});
            skArc(sketch, "E52.4.9", {"start": v(-31.84, 17.85) * mm, "mid": v(-30.66, 17.69) * mm, "end": v(-29.69, 18.4) * mm});
            skArc(sketch, "E52.5.0", {"start": v(-34.75, 3.47) * mm, "mid": v(-35.09, 4.62) * mm, "end": v(-36.13, 5.22) * mm});
            skLineSegment(sketch, "E52.5.1", {"start": v(-37.85, 5.45) * mm, "end": v(-36.13, 5.22) * mm});
            skArc(sketch, "E52.5.2", {"start": v(-37.85, 5.45) * mm, "mid": v(-39.19, 6.35) * mm, "end": v(-40.35, 7.47) * mm});
            skArc(sketch, "E52.5.3", {"start": v(-40.47, 7.87) * mm, "mid": v(-40.45, 7.65) * mm, "end": v(-40.35, 7.47) * mm});
            skLineSegment(sketch, "E52.5.4", {"start": v(-40.47, 7.87) * mm, "end": v(-40.45, 8.04) * mm});
            skLineSegment(sketch, "E52.5.5", {"start": v(-40.4, 8.2) * mm, "end": v(-40.45, 8.04) * mm});
            skArc(sketch, "E52.5.6", {"start": v(-40.14, 8.53) * mm, "mid": v(-40.3, 8.4) * mm, "end": v(-40.4, 8.2) * mm});
            skArc(sketch, "E52.5.7", {"start": v(-37.06, 9.44) * mm, "mid": v(-38.64, 9.12) * mm, "end": v(-40.14, 8.53) * mm});
            skLineSegment(sketch, "E52.5.8", {"start": v(-37.06, 9.44) * mm, "end": v(-35.38, 9) * mm});
            skArc(sketch, "E52.5.9", {"start": v(-35.38, 9) * mm, "mid": v(-34.19, 9.15) * mm, "end": v(-33.44, 10.08) * mm});
            skArc(sketch, "E52.6.0", {"start": v(-34.47, -5.64) * mm, "mid": v(-35.09, -4.62) * mm, "end": v(-36.25, -4.31) * mm});
            skLineSegment(sketch, "E52.6.1", {"start": v(-37.97, -4.53) * mm, "end": v(-36.25, -4.31) * mm});
            skArc(sketch, "E52.6.2", {"start": v(-37.97, -4.53) * mm, "mid": v(-39.5, -4) * mm, "end": v(-40.9, -3.23) * mm});
            skArc(sketch, "E52.6.3", {"start": v(-41.13, -2.88) * mm, "mid": v(-41.06, -3.08) * mm, "end": v(-40.9, -3.23) * mm});
            skLineSegment(sketch, "E52.6.4", {"start": v(-41.13, -2.88) * mm, "end": v(-41.15, -2.7) * mm});
            skLineSegment(sketch, "E52.6.5", {"start": v(-41.15, -2.53) * mm, "end": v(-41.15, -2.7) * mm});
            skArc(sketch, "E52.6.6", {"start": v(-40.98, -2.15) * mm, "mid": v(-41.1, -2.32) * mm, "end": v(-41.15, -2.53) * mm});
            skArc(sketch, "E52.6.7", {"start": v(-38.24, -0.47) * mm, "mid": v(-39.68, -1.2) * mm, "end": v(-40.98, -2.15) * mm});
            skLineSegment(sketch, "E52.6.8", {"start": v(-38.24, -0.47) * mm, "end": v(-36.5, -0.47) * mm});
            skArc(sketch, "E52.6.9", {"start": v(-36.5, -0.47) * mm, "mid": v(-35.4, -0.01) * mm, "end": v(-34.9, 1.08) * mm});
            skArc(sketch, "E52.7.0", {"start": v(-31.83, -14.37) * mm, "mid": v(-32.7, -13.54) * mm, "end": v(-33.9, -13.55) * mm});
            skLineSegment(sketch, "E52.7.1", {"start": v(-35.5, -14.2) * mm, "end": v(-33.9, -13.55) * mm});
            skArc(sketch, "E52.7.2", {"start": v(-35.5, -14.2) * mm, "mid": v(-37.11, -14.1) * mm, "end": v(-38.68, -13.7) * mm});
            skArc(sketch, "E52.7.3", {"start": v(-38.98, -13.42) * mm, "mid": v(-38.86, -13.6) * mm, "end": v(-38.68, -13.7) * mm});
            skLineSegment(sketch, "E52.7.4", {"start": v(-38.98, -13.42) * mm, "end": v(-39.05, -13.26) * mm});
            skLineSegment(sketch, "E52.7.5", {"start": v(-39.1, -13.1) * mm, "end": v(-39.05, -13.26) * mm});
            skArc(sketch, "E52.7.6", {"start": v(-39.03, -12.68) * mm, "mid": v(-39.1, -12.88) * mm, "end": v(-39.1, -13.1) * mm});
            skArc(sketch, "E52.7.7", {"start": v(-36.81, -10.35) * mm, "mid": v(-38.02, -11.42) * mm, "end": v(-39.03, -12.68) * mm});
            skLineSegment(sketch, "E52.7.8", {"start": v(-36.81, -10.35) * mm, "end": v(-35.14, -9.9) * mm});
            skArc(sketch, "E52.7.9", {"start": v(-35.14, -9.9) * mm, "mid": v(-34.18, -9.17) * mm, "end": v(-34, -7.99) * mm});
            skArc(sketch, "E52.8.0", {"start": v(-27.03, -22.12) * mm, "mid": v(-28.08, -21.54) * mm, "end": v(-29.24, -21.86) * mm});
            skLineSegment(sketch, "E52.8.1", {"start": v(-30.62, -22.91) * mm, "end": v(-29.24, -21.86) * mm});
            skArc(sketch, "E52.8.2", {"start": v(-30.62, -22.91) * mm, "mid": v(-32.2, -23.22) * mm, "end": v(-33.81, -23.25) * mm});
            skArc(sketch, "E52.8.3", {"start": v(-34.18, -23.05) * mm, "mid": v(-34.02, -23.2) * mm, "end": v(-33.81, -23.25) * mm});
            skLineSegment(sketch, "E52.8.4", {"start": v(-34.18, -23.05) * mm, "end": v(-34.29, -22.92) * mm});
            skLineSegment(sketch, "E52.8.5", {"start": v(-34.37, -22.77) * mm, "end": v(-34.29, -22.92) * mm});
            skArc(sketch, "E52.8.6", {"start": v(-34.42, -22.35) * mm, "mid": v(-34.44, -22.56) * mm, "end": v(-34.37, -22.77) * mm});
            skArc(sketch, "E52.8.7", {"start": v(-32.88, -19.53) * mm, "mid": v(-33.77, -20.87) * mm, "end": v(-34.42, -22.35) * mm});
            skLineSegment(sketch, "E52.8.8", {"start": v(-32.88, -19.53) * mm, "end": v(-31.38, -18.65) * mm});
            skArc(sketch, "E52.8.9", {"start": v(-31.38, -18.65) * mm, "mid": v(-30.64, -17.7) * mm, "end": v(-30.77, -16.51) * mm});
            skArc(sketch, "E52.9.0", {"start": v(-20.38, -28.36) * mm, "mid": v(-21.55, -28.08) * mm, "end": v(-22.58, -28.68) * mm});
            skLineSegment(sketch, "E52.9.1", {"start": v(-23.65, -30.06) * mm, "end": v(-22.58, -28.68) * mm});
            skArc(sketch, "E52.9.2", {"start": v(-23.65, -30.06) * mm, "mid": v(-25.1, -30.76) * mm, "end": v(-26.64, -31.21) * mm});
            skArc(sketch, "E52.9.3", {"start": v(-27.05, -31.12) * mm, "mid": v(-26.86, -31.2) * mm, "end": v(-26.64, -31.21) * mm});
            skLineSegment(sketch, "E52.9.4", {"start": v(-27.05, -31.12) * mm, "end": v(-27.19, -31.01) * mm});
            skLineSegment(sketch, "E52.9.5", {"start": v(-27.31, -30.89) * mm, "end": v(-27.19, -31.01) * mm});
            skArc(sketch, "E52.9.6", {"start": v(-27.46, -30.5) * mm, "mid": v(-27.43, -30.7) * mm, "end": v(-27.31, -30.89) * mm});
            skArc(sketch, "E52.9.7", {"start": v(-26.7, -27.37) * mm, "mid": v(-27.22, -28.9) * mm, "end": v(-27.46, -30.5) * mm});
            skLineSegment(sketch, "E52.9.8", {"start": v(-26.7, -27.37) * mm, "end": v(-25.48, -26.14) * mm});
            skArc(sketch, "E52.9.9", {"start": v(-25.48, -26.14) * mm, "mid": v(-25.02, -25.03) * mm, "end": v(-25.45, -23.92) * mm});
            skArc(sketch, "E52.10.0", {"start": v(-12.35, -32.67) * mm, "mid": v(-13.55, -32.7) * mm, "end": v(-14.39, -33.55) * mm});
            skLineSegment(sketch, "E52.10.1", {"start": v(-15.06, -35.15) * mm, "end": v(-14.39, -33.55) * mm});
            skArc(sketch, "E52.10.2", {"start": v(-15.06, -35.15) * mm, "mid": v(-16.28, -36.2) * mm, "end": v(-17.66, -37.04) * mm});
            skArc(sketch, "E52.10.3", {"start": v(-18.07, -37.06) * mm, "mid": v(-17.86, -37.1) * mm, "end": v(-17.66, -37.04) * mm});
            skLineSegment(sketch, "E52.10.4", {"start": v(-18.07, -37.06) * mm, "end": v(-18.24, -37) * mm});
            skLineSegment(sketch, "E52.10.5", {"start": v(-18.39, -36.9) * mm, "end": v(-18.24, -37) * mm});
            skArc(sketch, "E52.10.6", {"start": v(-18.63, -36.56) * mm, "mid": v(-18.54, -36.76) * mm, "end": v(-18.39, -36.9) * mm});
            skArc(sketch, "E52.10.7", {"start": v(-18.7, -33.35) * mm, "mid": v(-18.8, -34.96) * mm, "end": v(-18.63, -36.56) * mm});
            skLineSegment(sketch, "E52.10.8", {"start": v(-18.7, -33.35) * mm, "end": v(-17.85, -31.84) * mm});
            skArc(sketch, "E52.10.9", {"start": v(-17.85, -31.84) * mm, "mid": v(-17.69, -30.66) * mm, "end": v(-18.4, -29.69) * mm});
            skArc(sketch, "E52.11.0", {"start": v(-3.47, -34.75) * mm, "mid": v(-4.62, -35.09) * mm, "end": v(-5.22, -36.13) * mm});
            skLineSegment(sketch, "E52.11.1", {"start": v(-5.45, -37.85) * mm, "end": v(-5.22, -36.13) * mm});
            skArc(sketch, "E52.11.2", {"start": v(-5.45, -37.85) * mm, "mid": v(-6.35, -39.19) * mm, "end": v(-7.47, -40.35) * mm});
            skArc(sketch, "E52.11.3", {"start": v(-7.87, -40.47) * mm, "mid": v(-7.65, -40.45) * mm, "end": v(-7.47, -40.35) * mm});
            skLineSegment(sketch, "E52.11.4", {"start": v(-7.87, -40.47) * mm, "end": v(-8.04, -40.45) * mm});
            skLineSegment(sketch, "E52.11.5", {"start": v(-8.2, -40.4) * mm, "end": v(-8.04, -40.45) * mm});
            skArc(sketch, "E52.11.6", {"start": v(-8.53, -40.14) * mm, "mid": v(-8.4, -40.3) * mm, "end": v(-8.2, -40.4) * mm});
            skArc(sketch, "E52.11.7", {"start": v(-9.44, -37.06) * mm, "mid": v(-9.12, -38.64) * mm, "end": v(-8.53, -40.14) * mm});
            skLineSegment(sketch, "E52.11.8", {"start": v(-9.44, -37.06) * mm, "end": v(-9, -35.38) * mm});
            skArc(sketch, "E52.11.9", {"start": v(-9, -35.38) * mm, "mid": v(-9.15, -34.19) * mm, "end": v(-10.08, -33.44) * mm});
            skArc(sketch, "E52.12.0", {"start": v(5.64, -34.47) * mm, "mid": v(4.62, -35.09) * mm, "end": v(4.31, -36.25) * mm});
            skLineSegment(sketch, "E52.12.1", {"start": v(4.53, -37.97) * mm, "end": v(4.31, -36.25) * mm});
            skArc(sketch, "E52.12.2", {"start": v(4.53, -37.97) * mm, "mid": v(4, -39.5) * mm, "end": v(3.23, -40.9) * mm});
            skArc(sketch, "E52.12.3", {"start": v(2.88, -41.13) * mm, "mid": v(3.08, -41.06) * mm, "end": v(3.23, -40.9) * mm});
            skLineSegment(sketch, "E52.12.4", {"start": v(2.88, -41.13) * mm, "end": v(2.7, -41.15) * mm});
            skLineSegment(sketch, "E52.12.5", {"start": v(2.53, -41.15) * mm, "end": v(2.7, -41.15) * mm});
            skArc(sketch, "E52.12.6", {"start": v(2.15, -40.98) * mm, "mid": v(2.32, -41.1) * mm, "end": v(2.53, -41.15) * mm});
            skArc(sketch, "E52.12.7", {"start": v(0.47, -38.24) * mm, "mid": v(1.2, -39.68) * mm, "end": v(2.15, -40.98) * mm});
            skLineSegment(sketch, "E52.12.8", {"start": v(0.47, -38.24) * mm, "end": v(0.47, -36.5) * mm});
            skArc(sketch, "E52.12.9", {"start": v(0.47, -36.5) * mm, "mid": v(0.01, -35.4) * mm, "end": v(-1.08, -34.9) * mm});
            skArc(sketch, "E52.13.0", {"start": v(14.37, -31.83) * mm, "mid": v(13.54, -32.7) * mm, "end": v(13.55, -33.9) * mm});
            skLineSegment(sketch, "E52.13.1", {"start": v(14.2, -35.5) * mm, "end": v(13.55, -33.9) * mm});
            skArc(sketch, "E52.13.2", {"start": v(14.2, -35.5) * mm, "mid": v(14.1, -37.11) * mm, "end": v(13.7, -38.68) * mm});
            skArc(sketch, "E52.13.3", {"start": v(13.42, -38.98) * mm, "mid": v(13.6, -38.86) * mm, "end": v(13.7, -38.68) * mm});
            skLineSegment(sketch, "E52.13.4", {"start": v(13.42, -38.98) * mm, "end": v(13.26, -39.05) * mm});
            skLineSegment(sketch, "E52.13.5", {"start": v(13.1, -39.1) * mm, "end": v(13.26, -39.05) * mm});
            skArc(sketch, "E52.13.6", {"start": v(12.68, -39.03) * mm, "mid": v(12.88, -39.1) * mm, "end": v(13.1, -39.1) * mm});
            skArc(sketch, "E52.13.7", {"start": v(10.35, -36.81) * mm, "mid": v(11.42, -38.02) * mm, "end": v(12.68, -39.03) * mm});
            skLineSegment(sketch, "E52.13.8", {"start": v(10.35, -36.81) * mm, "end": v(9.9, -35.14) * mm});
            skArc(sketch, "E52.13.9", {"start": v(9.9, -35.14) * mm, "mid": v(9.17, -34.18) * mm, "end": v(7.99, -34) * mm});
            skArc(sketch, "E52.14.0", {"start": v(22.12, -27.03) * mm, "mid": v(21.54, -28.08) * mm, "end": v(21.86, -29.24) * mm});
            skLineSegment(sketch, "E52.14.1", {"start": v(22.91, -30.62) * mm, "end": v(21.86, -29.24) * mm});
            skArc(sketch, "E52.14.2", {"start": v(22.91, -30.62) * mm, "mid": v(23.22, -32.2) * mm, "end": v(23.25, -33.81) * mm});
            skArc(sketch, "E52.14.3", {"start": v(23.05, -34.18) * mm, "mid": v(23.2, -34.02) * mm, "end": v(23.25, -33.81) * mm});
            skLineSegment(sketch, "E52.14.4", {"start": v(23.05, -34.18) * mm, "end": v(22.92, -34.29) * mm});
            skLineSegment(sketch, "E52.14.5", {"start": v(22.77, -34.37) * mm, "end": v(22.92, -34.29) * mm});
            skArc(sketch, "E52.14.6", {"start": v(22.35, -34.42) * mm, "mid": v(22.56, -34.44) * mm, "end": v(22.77, -34.37) * mm});
            skArc(sketch, "E52.14.7", {"start": v(19.53, -32.88) * mm, "mid": v(20.87, -33.77) * mm, "end": v(22.35, -34.42) * mm});
            skLineSegment(sketch, "E52.14.8", {"start": v(19.53, -32.88) * mm, "end": v(18.65, -31.38) * mm});
            skArc(sketch, "E52.14.9", {"start": v(18.65, -31.38) * mm, "mid": v(17.7, -30.64) * mm, "end": v(16.51, -30.77) * mm});
            skArc(sketch, "E52.15.0", {"start": v(28.36, -20.38) * mm, "mid": v(28.08, -21.55) * mm, "end": v(28.68, -22.58) * mm});
            skLineSegment(sketch, "E52.15.1", {"start": v(30.06, -23.65) * mm, "end": v(28.68, -22.58) * mm});
            skArc(sketch, "E52.15.2", {"start": v(30.06, -23.65) * mm, "mid": v(30.76, -25.1) * mm, "end": v(31.21, -26.64) * mm});
            skArc(sketch, "E52.15.3", {"start": v(31.12, -27.05) * mm, "mid": v(31.2, -26.86) * mm, "end": v(31.21, -26.64) * mm});
            skLineSegment(sketch, "E52.15.4", {"start": v(31.12, -27.05) * mm, "end": v(31.01, -27.19) * mm});
            skLineSegment(sketch, "E52.15.5", {"start": v(30.89, -27.31) * mm, "end": v(31.01, -27.19) * mm});
            skArc(sketch, "E52.15.6", {"start": v(30.5, -27.46) * mm, "mid": v(30.7, -27.43) * mm, "end": v(30.89, -27.31) * mm});
            skArc(sketch, "E52.15.7", {"start": v(27.37, -26.7) * mm, "mid": v(28.9, -27.22) * mm, "end": v(30.5, -27.46) * mm});
            skLineSegment(sketch, "E52.15.8", {"start": v(27.37, -26.7) * mm, "end": v(26.14, -25.48) * mm});
            skArc(sketch, "E52.15.9", {"start": v(26.14, -25.48) * mm, "mid": v(25.03, -25.02) * mm, "end": v(23.92, -25.45) * mm});
            skArc(sketch, "E52.16.0", {"start": v(32.67, -12.35) * mm, "mid": v(32.7, -13.55) * mm, "end": v(33.55, -14.39) * mm});
            skLineSegment(sketch, "E52.16.1", {"start": v(35.15, -15.06) * mm, "end": v(33.55, -14.39) * mm});
            skArc(sketch, "E52.16.2", {"start": v(35.15, -15.06) * mm, "mid": v(36.2, -16.28) * mm, "end": v(37.04, -17.66) * mm});
            skArc(sketch, "E52.16.3", {"start": v(37.06, -18.07) * mm, "mid": v(37.1, -17.86) * mm, "end": v(37.04, -17.66) * mm});
            skLineSegment(sketch, "E52.16.4", {"start": v(37.06, -18.07) * mm, "end": v(37, -18.24) * mm});
            skLineSegment(sketch, "E52.16.5", {"start": v(36.9, -18.39) * mm, "end": v(37, -18.24) * mm});
            skArc(sketch, "E52.16.6", {"start": v(36.56, -18.63) * mm, "mid": v(36.76, -18.54) * mm, "end": v(36.9, -18.39) * mm});
            skArc(sketch, "E52.16.7", {"start": v(33.35, -18.7) * mm, "mid": v(34.96, -18.8) * mm, "end": v(36.56, -18.63) * mm});
            skLineSegment(sketch, "E52.16.8", {"start": v(33.35, -18.7) * mm, "end": v(31.84, -17.85) * mm});
            skArc(sketch, "E52.16.9", {"start": v(31.84, -17.85) * mm, "mid": v(30.66, -17.69) * mm, "end": v(29.69, -18.4) * mm});
            skArc(sketch, "E52.17.0", {"start": v(34.75, -3.47) * mm, "mid": v(35.09, -4.62) * mm, "end": v(36.13, -5.22) * mm});
            skLineSegment(sketch, "E52.17.1", {"start": v(37.85, -5.45) * mm, "end": v(36.13, -5.22) * mm});
            skArc(sketch, "E52.17.2", {"start": v(37.85, -5.45) * mm, "mid": v(39.19, -6.35) * mm, "end": v(40.35, -7.47) * mm});
            skArc(sketch, "E52.17.3", {"start": v(40.47, -7.87) * mm, "mid": v(40.45, -7.65) * mm, "end": v(40.35, -7.47) * mm});
            skLineSegment(sketch, "E52.17.4", {"start": v(40.47, -7.87) * mm, "end": v(40.45, -8.04) * mm});
            skLineSegment(sketch, "E52.17.5", {"start": v(40.4, -8.2) * mm, "end": v(40.45, -8.04) * mm});
            skArc(sketch, "E52.17.6", {"start": v(40.14, -8.53) * mm, "mid": v(40.3, -8.4) * mm, "end": v(40.4, -8.2) * mm});
            skArc(sketch, "E52.17.7", {"start": v(37.06, -9.44) * mm, "mid": v(38.64, -9.12) * mm, "end": v(40.14, -8.53) * mm});
            skLineSegment(sketch, "E52.17.8", {"start": v(37.06, -9.44) * mm, "end": v(35.38, -9) * mm});
            skArc(sketch, "E52.17.9", {"start": v(35.38, -9) * mm, "mid": v(34.19, -9.15) * mm, "end": v(33.44, -10.08) * mm});
            skArc(sketch, "E52.18.0", {"start": v(34.47, 5.64) * mm, "mid": v(35.09, 4.62) * mm, "end": v(36.25, 4.31) * mm});
            skLineSegment(sketch, "E52.18.1", {"start": v(37.97, 4.53) * mm, "end": v(36.25, 4.31) * mm});
            skArc(sketch, "E52.18.2", {"start": v(37.97, 4.53) * mm, "mid": v(39.5, 4) * mm, "end": v(40.9, 3.23) * mm});
            skArc(sketch, "E52.18.3", {"start": v(41.13, 2.88) * mm, "mid": v(41.06, 3.08) * mm, "end": v(40.9, 3.23) * mm});
            skLineSegment(sketch, "E52.18.4", {"start": v(41.13, 2.88) * mm, "end": v(41.15, 2.7) * mm});
            skLineSegment(sketch, "E52.18.5", {"start": v(41.15, 2.53) * mm, "end": v(41.15, 2.7) * mm});
            skArc(sketch, "E52.18.6", {"start": v(40.98, 2.15) * mm, "mid": v(41.1, 2.32) * mm, "end": v(41.15, 2.53) * mm});
            skArc(sketch, "E52.18.7", {"start": v(38.24, 0.47) * mm, "mid": v(39.68, 1.2) * mm, "end": v(40.98, 2.15) * mm});
            skLineSegment(sketch, "E52.18.8", {"start": v(38.24, 0.47) * mm, "end": v(36.5, 0.47) * mm});
            skArc(sketch, "E52.18.9", {"start": v(36.5, 0.47) * mm, "mid": v(35.4, 0.01) * mm, "end": v(34.9, -1.08) * mm});
            skArc(sketch, "E52.19.0", {"start": v(31.83, 14.37) * mm, "mid": v(32.7, 13.54) * mm, "end": v(33.9, 13.55) * mm});
            skLineSegment(sketch, "E52.19.1", {"start": v(35.5, 14.2) * mm, "end": v(33.9, 13.55) * mm});
            skArc(sketch, "E52.19.2", {"start": v(35.5, 14.2) * mm, "mid": v(37.11, 14.1) * mm, "end": v(38.68, 13.7) * mm});
            skArc(sketch, "E52.19.3", {"start": v(38.98, 13.42) * mm, "mid": v(38.86, 13.6) * mm, "end": v(38.68, 13.7) * mm});
            skLineSegment(sketch, "E52.19.4", {"start": v(38.98, 13.42) * mm, "end": v(39.05, 13.26) * mm});
            skLineSegment(sketch, "E52.19.5", {"start": v(39.1, 13.1) * mm, "end": v(39.05, 13.26) * mm});
            skArc(sketch, "E52.19.6", {"start": v(39.03, 12.68) * mm, "mid": v(39.1, 12.88) * mm, "end": v(39.1, 13.1) * mm});
            skArc(sketch, "E52.19.7", {"start": v(36.81, 10.35) * mm, "mid": v(38.02, 11.42) * mm, "end": v(39.03, 12.68) * mm});
            skLineSegment(sketch, "E52.19.8", {"start": v(36.81, 10.35) * mm, "end": v(35.14, 9.9) * mm});
            skArc(sketch, "E52.19.9", {"start": v(35.14, 9.9) * mm, "mid": v(34.18, 9.17) * mm, "end": v(34, 7.99) * mm});
            skArc(sketch, "E52.20.0", {"start": v(27.03, 22.12) * mm, "mid": v(28.08, 21.54) * mm, "end": v(29.24, 21.86) * mm});
            skLineSegment(sketch, "E52.20.1", {"start": v(30.62, 22.91) * mm, "end": v(29.24, 21.86) * mm});
            skArc(sketch, "E52.20.2", {"start": v(30.62, 22.91) * mm, "mid": v(32.2, 23.22) * mm, "end": v(33.81, 23.25) * mm});
            skArc(sketch, "E52.20.3", {"start": v(34.18, 23.05) * mm, "mid": v(34.02, 23.2) * mm, "end": v(33.81, 23.25) * mm});
            skLineSegment(sketch, "E52.20.4", {"start": v(34.18, 23.05) * mm, "end": v(34.29, 22.92) * mm});
            skLineSegment(sketch, "E52.20.5", {"start": v(34.37, 22.77) * mm, "end": v(34.29, 22.92) * mm});
            skArc(sketch, "E52.20.6", {"start": v(34.42, 22.35) * mm, "mid": v(34.44, 22.56) * mm, "end": v(34.37, 22.77) * mm});
            skArc(sketch, "E52.20.7", {"start": v(32.88, 19.53) * mm, "mid": v(33.77, 20.87) * mm, "end": v(34.42, 22.35) * mm});
            skLineSegment(sketch, "E52.20.8", {"start": v(32.88, 19.53) * mm, "end": v(31.38, 18.65) * mm});
            skArc(sketch, "E52.20.9", {"start": v(31.38, 18.65) * mm, "mid": v(30.64, 17.7) * mm, "end": v(30.77, 16.51) * mm});
            skArc(sketch, "E52.21.0", {"start": v(20.38, 28.36) * mm, "mid": v(21.55, 28.08) * mm, "end": v(22.58, 28.68) * mm});
            skLineSegment(sketch, "E52.21.1", {"start": v(23.65, 30.06) * mm, "end": v(22.58, 28.68) * mm});
            skArc(sketch, "E52.21.2", {"start": v(23.65, 30.06) * mm, "mid": v(25.1, 30.76) * mm, "end": v(26.64, 31.21) * mm});
            skArc(sketch, "E52.21.3", {"start": v(27.05, 31.12) * mm, "mid": v(26.86, 31.2) * mm, "end": v(26.64, 31.21) * mm});
            skLineSegment(sketch, "E52.21.4", {"start": v(27.05, 31.12) * mm, "end": v(27.19, 31.01) * mm});
            skLineSegment(sketch, "E52.21.5", {"start": v(27.31, 30.89) * mm, "end": v(27.19, 31.01) * mm});
            skArc(sketch, "E52.21.6", {"start": v(27.46, 30.5) * mm, "mid": v(27.43, 30.7) * mm, "end": v(27.31, 30.89) * mm});
            skArc(sketch, "E52.21.7", {"start": v(26.7, 27.37) * mm, "mid": v(27.22, 28.9) * mm, "end": v(27.46, 30.5) * mm});
            skLineSegment(sketch, "E52.21.8", {"start": v(26.7, 27.37) * mm, "end": v(25.48, 26.14) * mm});
            skArc(sketch, "E52.21.9", {"start": v(25.48, 26.14) * mm, "mid": v(25.02, 25.03) * mm, "end": v(25.45, 23.92) * mm});
            skArc(sketch, "E52.22.0", {"start": v(12.35, 32.67) * mm, "mid": v(13.55, 32.7) * mm, "end": v(14.39, 33.55) * mm});
            skLineSegment(sketch, "E52.22.1", {"start": v(15.06, 35.15) * mm, "end": v(14.39, 33.55) * mm});
            skArc(sketch, "E52.22.2", {"start": v(15.06, 35.15) * mm, "mid": v(16.28, 36.2) * mm, "end": v(17.66, 37.04) * mm});
            skArc(sketch, "E52.22.3", {"start": v(18.07, 37.06) * mm, "mid": v(17.86, 37.1) * mm, "end": v(17.66, 37.04) * mm});
            skLineSegment(sketch, "E52.22.4", {"start": v(18.07, 37.06) * mm, "end": v(18.24, 37) * mm});
            skLineSegment(sketch, "E52.22.5", {"start": v(18.39, 36.9) * mm, "end": v(18.24, 37) * mm});
            skArc(sketch, "E52.22.6", {"start": v(18.63, 36.56) * mm, "mid": v(18.54, 36.76) * mm, "end": v(18.39, 36.9) * mm});
            skArc(sketch, "E52.22.7", {"start": v(18.7, 33.35) * mm, "mid": v(18.8, 34.96) * mm, "end": v(18.63, 36.56) * mm});
            skLineSegment(sketch, "E52.22.8", {"start": v(18.7, 33.35) * mm, "end": v(17.85, 31.84) * mm});
            skArc(sketch, "E52.22.9", {"start": v(17.85, 31.84) * mm, "mid": v(17.69, 30.66) * mm, "end": v(18.4, 29.69) * mm});
            skArc(sketch, "E52.23.0", {"start": v(3.47, 34.75) * mm, "mid": v(4.62, 35.09) * mm, "end": v(5.22, 36.13) * mm});
            skLineSegment(sketch, "E52.23.1", {"start": v(5.45, 37.85) * mm, "end": v(5.22, 36.13) * mm});
            skArc(sketch, "E52.23.2", {"start": v(5.45, 37.85) * mm, "mid": v(6.35, 39.19) * mm, "end": v(7.47, 40.35) * mm});
            skArc(sketch, "E52.23.3", {"start": v(7.87, 40.47) * mm, "mid": v(7.65, 40.45) * mm, "end": v(7.47, 40.35) * mm});
            skLineSegment(sketch, "E52.23.4", {"start": v(7.87, 40.47) * mm, "end": v(8.04, 40.45) * mm});
            skLineSegment(sketch, "E52.23.5", {"start": v(8.2, 40.4) * mm, "end": v(8.04, 40.45) * mm});
            skArc(sketch, "E52.23.6", {"start": v(8.53, 40.14) * mm, "mid": v(8.4, 40.3) * mm, "end": v(8.2, 40.4) * mm});
            skArc(sketch, "E52.23.7", {"start": v(9.44, 37.06) * mm, "mid": v(9.12, 38.64) * mm, "end": v(8.53, 40.14) * mm});
            skLineSegment(sketch, "E52.23.8", {"start": v(9.44, 37.06) * mm, "end": v(9, 35.38) * mm});
            skArc(sketch, "E52.23.9", {"start": v(9, 35.38) * mm, "mid": v(9.15, 34.19) * mm, "end": v(10.08, 33.44) * mm});
            skArc(sketch, "E53.trimOffspring", {"start": v(-14.37, 31.83) * mm, "mid": v(-15.45, 31.32) * mm, "end": v(-16.51, 30.77) * mm});
            skArc(sketch, "E54.trimOffspring", {"start": v(-22.12, 27.03) * mm, "mid": v(-23.03, 26.25) * mm, "end": v(-23.92, 25.45) * mm});
            skArc(sketch, "E55.trimOffspring", {"start": v(-28.36, 20.38) * mm, "mid": v(-29.04, 19.4) * mm, "end": v(-29.69, 18.4) * mm});
            skArc(sketch, "E56.trimOffspring", {"start": v(-32.67, 12.35) * mm, "mid": v(-33.07, 11.22) * mm, "end": v(-33.44, 10.08) * mm});
            skArc(sketch, "E57.trimOffspring", {"start": v(-34.75, 3.47) * mm, "mid": v(-34.85, 2.28) * mm, "end": v(-34.9, 1.08) * mm});
            skArc(sketch, "E58.trimOffspring", {"start": v(-34.47, -5.64) * mm, "mid": v(-34.25, -6.82) * mm, "end": v(-34, -7.99) * mm});
            skArc(sketch, "E59.trimOffspring", {"start": v(-31.83, -14.37) * mm, "mid": v(-31.32, -15.45) * mm, "end": v(-30.77, -16.51) * mm});
            skArc(sketch, "E60.trimOffspring", {"start": v(-27.03, -22.12) * mm, "mid": v(-26.25, -23.03) * mm, "end": v(-25.45, -23.92) * mm});
            skArc(sketch, "E61.trimOffspring", {"start": v(-20.38, -28.36) * mm, "mid": v(-19.4, -29.04) * mm, "end": v(-18.4, -29.69) * mm});
            skArc(sketch, "E62.trimOffspring", {"start": v(-12.35, -32.67) * mm, "mid": v(-11.22, -33.07) * mm, "end": v(-10.08, -33.44) * mm});
            skArc(sketch, "E63.trimOffspring", {"start": v(-3.47, -34.75) * mm, "mid": v(-2.28, -34.85) * mm, "end": v(-1.08, -34.9) * mm});
            skArc(sketch, "E64.trimOffspring", {"start": v(5.64, -34.47) * mm, "mid": v(6.82, -34.25) * mm, "end": v(7.99, -34) * mm});
            skArc(sketch, "E65.trimOffspring", {"start": v(14.37, -31.83) * mm, "mid": v(15.45, -31.32) * mm, "end": v(16.51, -30.77) * mm});
            skArc(sketch, "E66.trimOffspring", {"start": v(22.12, -27.03) * mm, "mid": v(23.03, -26.25) * mm, "end": v(23.92, -25.45) * mm});
            skArc(sketch, "E67.trimOffspring", {"start": v(28.36, -20.38) * mm, "mid": v(29.04, -19.4) * mm, "end": v(29.69, -18.4) * mm});
            skArc(sketch, "E68.trimOffspring", {"start": v(32.67, -12.35) * mm, "mid": v(33.07, -11.22) * mm, "end": v(33.44, -10.08) * mm});
            skArc(sketch, "E69.trimOffspring", {"start": v(34.75, -3.47) * mm, "mid": v(34.85, -2.28) * mm, "end": v(34.9, -1.08) * mm});
            skArc(sketch, "E70.trimOffspring", {"start": v(34.47, 5.64) * mm, "mid": v(34.25, 6.82) * mm, "end": v(34, 7.99) * mm});
            skArc(sketch, "E71.trimOffspring", {"start": v(31.83, 14.37) * mm, "mid": v(31.32, 15.45) * mm, "end": v(30.77, 16.51) * mm});
            skArc(sketch, "E72.trimOffspring", {"start": v(27.03, 22.12) * mm, "mid": v(26.25, 23.03) * mm, "end": v(25.45, 23.92) * mm});
            skArc(sketch, "E73.trimOffspring", {"start": v(20.38, 28.36) * mm, "mid": v(19.4, 29.04) * mm, "end": v(18.4, 29.69) * mm});
            skArc(sketch, "E74.trimOffspring", {"start": v(12.35, 32.67) * mm, "mid": v(11.22, 33.07) * mm, "end": v(10.08, 33.44) * mm});
            skArc(sketch, "E75.trimOffspring", {"start": v(3.47, 34.75) * mm, "mid": v(2.28, 34.85) * mm, "end": v(1.08, 34.9) * mm});
            skSolve(sketch);
        }
        {
            var Q0;
            Q0=makeQuery(id+"F0.imprint","IMPRINT",FACE,{"disambiguationData":[TD([[makeQuery(id+"F0.imprint","IMPRINT",EDGE,{"derivedFrom":sQuery(id+"F0.wireOp",EDGE,"E0")}),1.0]])]});
            var Q1;
            Q1=makeQuery(id+"F2.imprint","IMPRINT",FACE,{"disambiguationData":[TD([[makeQuery(id+"F2.imprint","IMPRINT",EDGE,{"derivedFrom":sQuery(id+"F2.wireOp",EDGE,"E38")}),1.0]])]});
            var Q2;
            Q2=sQuery(id+"F0.wireOp",VERTEX,"E5.MirrorCS.start");
            var Q3;
            Q3=sQuery(id+"F2.wireOp",VERTEX,"E52.1.4.start");
            loft(context, id + "F3", {"sheetProfilesArray" : [{ "sheetProfileEntities" : qUnion([Q0]) }, { "sheetProfileEntities" : qUnion([Q1]) }], "matchConnections" : true, "connections" : [{ "connectionEntities" : qUnion([Q2, Q3]), "connectionEdgeQueries" : qUnion([]), "connectionEdgeParameters" : [] }]});
        }
        {
            var Q0;
            Q0=makeQuery(id+"F3.opLoft","CAP_FACE",FACE,{"disambiguationData":[OSD([makeQuery(id+"F2.imprint","IMPRINT",FACE,{"disambiguationData":[TD([[makeQuery(id+"F2.imprint","IMPRINT",EDGE,{"derivedFrom":sQuery(id+"F2.wireOp",EDGE,"E38")}),1.0]])]})])],"isStart":true});
            var sketch = newSketch(context, id + "F4", { "sketchPlane" : qUnion([Q0])});
            skCircle(sketch, "E76", {"center": v(0, 0) * mm, "radius": 6.35 * mm});
            skSolve(sketch);
        }
        {
            var Q0;
            Q0 = qSketchRegion(id + "F4", true);
            extrude(context, id + "F5", {"entities" : qUnion([Q0]), "operationType" : NewBodyOperationType.REMOVE, "endBound" : BoundingType.THROUGH_ALL, "oppositeDirection" : true, "depth" : 25.4 * mm});
        }
    });
